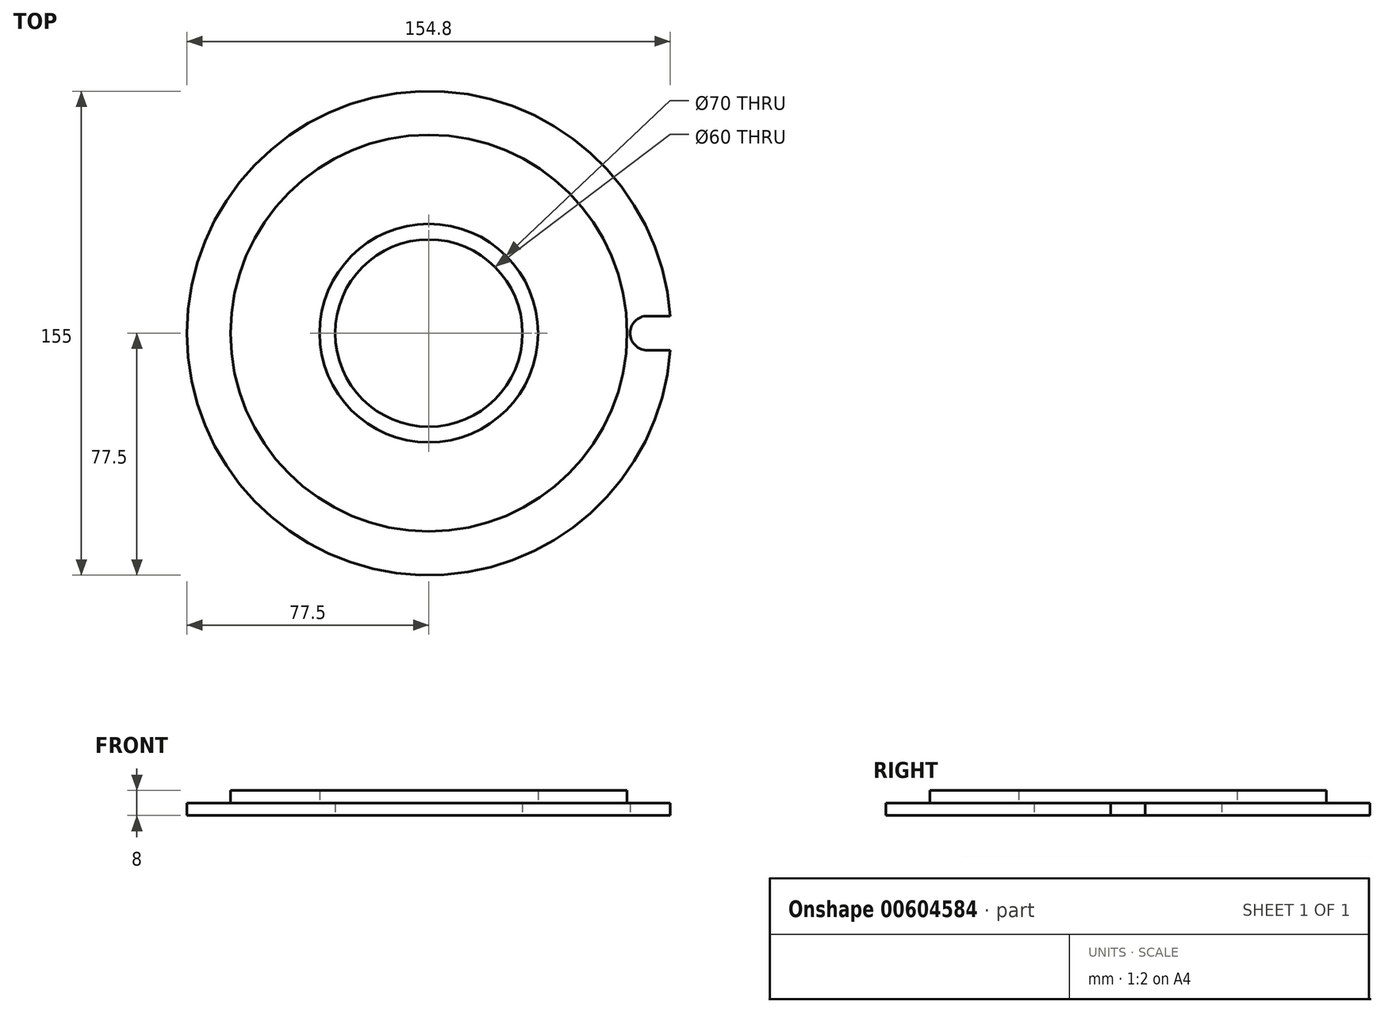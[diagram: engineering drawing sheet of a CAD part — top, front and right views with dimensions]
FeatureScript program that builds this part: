
annotation { "Feature Type Name" : "Feature", "Feature Type Description" : "" }
export const myFeature = defineFeature(function(context is Context, id is Id, definition is map)
    precondition{}
    {
        {
            var Q0;
            Q0=qCreatedBy(makeId("Top.planeOp"),FACE);
            var sketch = newSketch(context, id + "F0", { "sketchPlane" : qUnion([Q0])});
            skCircle(sketch, "E0", {"center": v(0, 0) * mm, "radius": 77.5 * mm});
            skCircle(sketch, "E1", {"center": v(0, 0) * mm, "radius": 30 * mm});
            skLineSegment(sketch, "E2", {"start": v(0, 0) * mm, "end": v(96.46, 0) * mm, "construction": true});
            skCircle(sketch, "E3", {"center": v(70, 0) * mm, "radius": 5.5 * mm});
            skLineSegment(sketch, "E4", {"start": v(70, 0) * mm, "end": v(70, 8.5) * mm});
            skLineSegment(sketch, "E5", {"start": v(70, 5.5) * mm, "end": v(77.3, 5.5) * mm});
            skLineSegment(sketch, "E6", {"start": v(70, -5.5) * mm, "end": v(77.3, -5.5) * mm});
            skSolve(sketch);
        }
        {
            var Q0;
            Q0=makeQuery(id+"F0.imprint","IMPRINT",FACE,{"disambiguationData":[TD([[makeQuery(id+"F0.imprint","IMPRINT",EDGE,{"derivedFrom":sQuery(id+"F0.wireOp",EDGE,"E1")}),-1.0]])]});
            var Q1;
            {var subQ0=sQuery(id+"F0.wireOp",EDGE,"E5");Q1=makeQuery(id+"F0.imprint","IMPRINT",FACE,{"disambiguationData":[TD([[makeQuery(id+"F0.imprint","IMPRINT",EDGE,{"derivedFrom":subQ0}),-1.0]])]});}
            var Q2;
            {var subQ0=sQuery(id+"F0.wireOp",EDGE,"E3");var subQ1=makeQuery(id+"F0.imprint","INTERSECT",VERTEX,{"derivedFrom":[subQ0,sQuery(id+"F0.wireOp",EDGE,"E5")]});Q2=makeQuery(id+"F0.imprint","IMPRINT",FACE,{"disambiguationData":[TD([[makeQuery(id+"F0.imprint","IMPRINT",EDGE,{"disambiguationData":[TD([[subQ1,-1.0]])],"derivedFrom":subQ0}),1.0]])]});}
            extrude(context, id + "F1", {"entities" : qUnion([Q0, Q1, Q2]), "depth" : 4 * mm, "offsetDistance" : 25 * mm});
        }
        {
            var Q0;
            {var subQ0=sQuery(id+"F0.wireOp",EDGE,"E3");var subQ1=makeQuery(id+"F0.imprint","INTERSECT",VERTEX,{"derivedFrom":[subQ0,sQuery(id+"F0.wireOp",EDGE,"E5")]});Q0=makeQuery(id+"F0.imprint","IMPRINT",FACE,{"disambiguationData":[TD([[makeQuery(id+"F0.imprint","IMPRINT",EDGE,{"disambiguationData":[TD([[subQ1,-1.0]])],"derivedFrom":subQ0}),1.0]])]});}
            var Q1;
            {var subQ0=sQuery(id+"F0.wireOp",EDGE,"E5");Q1=makeQuery(id+"F0.imprint","IMPRINT",FACE,{"disambiguationData":[TD([[makeQuery(id+"F0.imprint","IMPRINT",EDGE,{"derivedFrom":subQ0}),-1.0]])]});}
            extrude(context, id + "F2", {"entities" : qUnion([Q0, Q1]), "operationType" : NewBodyOperationType.REMOVE, "depth" : 25 * mm, "offsetDistance" : 25 * mm});
        }
        {
            var Q0;
            Q0=qCreatedBy(makeId("Right.planeOp"),FACE);
            var sketch = newSketch(context, id + "F3", { "sketchPlane" : qUnion([Q0])});
            skLineSegment(sketch, "E7", {"start": v(0, 0) * mm, "end": v(0, 82.2) * mm});
            skSolve(sketch);
        }
        {
            var Q0;
            Q0=makeQuery(id+"F1.opExtrude","CAP_FACE",FACE,{"disambiguationData":[OSD([sQuery(id+"F0.wireOp",EDGE,"E0"),sQuery(id+"F0.wireOp",EDGE,"E1")])],"isStart":false});
            var sketch = newSketch(context, id + "F4", { "sketchPlane" : qUnion([Q0])});
            skCircle(sketch, "E8", {"center": v(0, 0) * mm, "radius": 63.5 * mm});
            skCircle(sketch, "E9", {"center": v(0, 0) * mm, "radius": 35 * mm});
            skSolve(sketch);
        }
        {
            var Q0;
            Q0=makeQuery(id+"F4.imprint","IMPRINT",FACE,{"disambiguationData":[TD([[makeQuery(id+"F4.imprint","IMPRINT",EDGE,{"derivedFrom":sQuery(id+"F4.wireOp",EDGE,"E8")}),1.0]])]});
            extrude(context, id + "F5", {"entities" : qUnion([Q0]), "depth" : 4 * mm, "offsetDistance" : 25 * mm});
        }
    });
